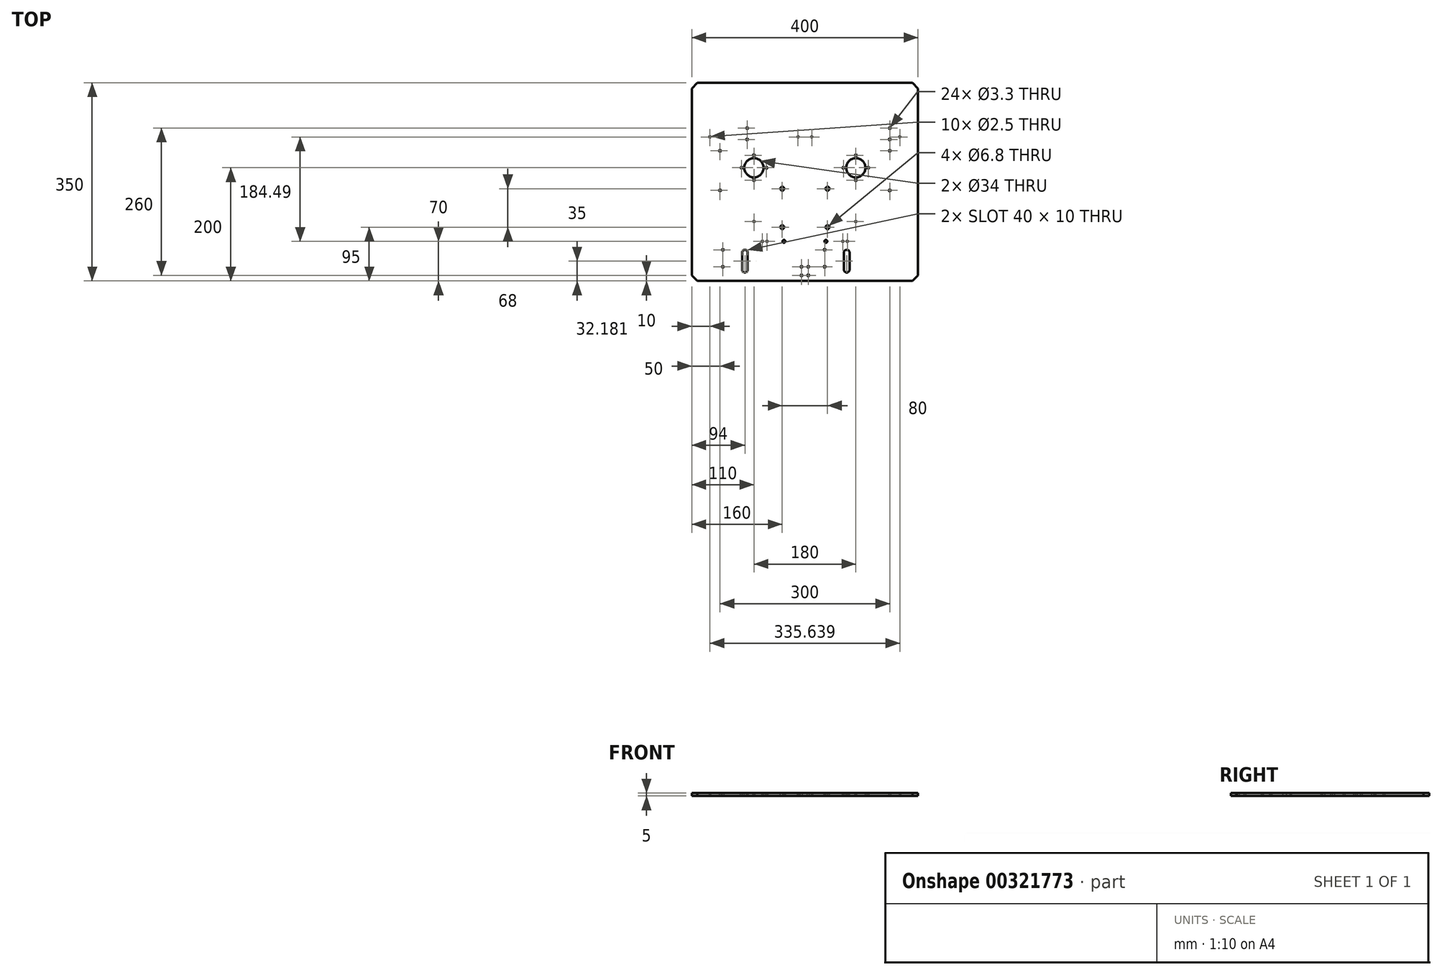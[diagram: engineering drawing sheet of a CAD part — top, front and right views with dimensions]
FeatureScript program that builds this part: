
annotation { "Feature Type Name" : "Feature", "Feature Type Description" : "" }
export const myFeature = defineFeature(function(context is Context, id is Id, definition is map)
    precondition{}
    {
        {
            var Q0;
            Q0=qCreatedBy(makeId("Top.planeOp"),FACE);
            var sketch = newSketch(context, id + "F0", { "sketchPlane" : qUnion([Q0])});
            skLineSegment(sketch, "E0.bottom", {"start": v(-200, 100) * mm, "end": v(200, 100) * mm});
            skLineSegment(sketch, "E0.top", {"start": v(-200, -250) * mm, "end": v(200, -250) * mm});
            skLineSegment(sketch, "E0.left", {"start": v(-200, 100) * mm, "end": v(-200, -250) * mm});
            skLineSegment(sketch, "E0.right", {"start": v(200, 100) * mm, "end": v(200, -250) * mm});
            skSolve(sketch);
        }
        {
            var Q0;
            Q0=qSketchRegion(id+"F0",true);
            extrude(context, id + "F1", {"entities" : qUnion([Q0]), "depth" : 5 * mm});
        }
        {
            var Q0;
            Q0=makeQuery(id+"F1.opExtrude","CAP_FACE",FACE,{"disambiguationData":[OSD([sQuery(id+"F0.wireOp",EDGE,"E0.bottom"),sQuery(id+"F0.wireOp",EDGE,"E0.top"),sQuery(id+"F0.wireOp",EDGE,"E0.left"),sQuery(id+"F0.wireOp",EDGE,"E0.right")])],"isStart":false});
            var sketch = newSketch(context, id + "F2", { "sketchPlane" : qUnion([Q0])});
            skCircle(sketch, "E1", {"center": v(-90, -50) * mm, "radius": 17 * mm});
            skCircle(sketch, "E2", {"center": v(90, -50) * mm, "radius": 17 * mm});
            skSolve(sketch);
        }
        {
            var Q0;
            Q0=qSketchRegion(id+"F2",true);
            extrude(context, id + "F3", {"entities" : qUnion([Q0]), "operationType" : NewBodyOperationType.REMOVE, "oppositeDirection" : true, "depth" : 25 * mm});
        }
        {
            var Q0;
            Q0=makeQuery(id+"F1.opExtrude","CAP_FACE",FACE,{"disambiguationData":[OSD([sQuery(id+"F0.wireOp",EDGE,"E0.bottom"),sQuery(id+"F0.wireOp",EDGE,"E0.top"),sQuery(id+"F0.wireOp",EDGE,"E0.left"),sQuery(id+"F0.wireOp",EDGE,"E0.right")])],"isStart":false});
            var sketch = newSketch(context, id + "F4", { "sketchPlane" : qUnion([Q0])});
            skCircle(sketch, "E3", {"center": v(-90, -50) * mm, "radius": 22 * mm});
            skCircle(sketch, "E4", {"center": v(90, -50) * mm, "radius": 22 * mm});
            skPoint(sketch, "E5", {"position": v(90, -28) * mm});
            skPoint(sketch, "E6", {"position": v(112, -50) * mm});
            skPoint(sketch, "E7", {"position": v(90, -72) * mm});
            skPoint(sketch, "E8", {"position": v(68, -50) * mm});
            skPoint(sketch, "E9", {"position": v(-68, -50) * mm});
            skPoint(sketch, "E10", {"position": v(-90, -28) * mm});
            skPoint(sketch, "E11", {"position": v(-90, -72) * mm});
            skPoint(sketch, "E12", {"position": v(-112, -50) * mm});
            skSolve(sketch);
        }
        {
            var Q0;
            Q0=sQuery(id+"F4.wireOp",VERTEX,"E11");
            var Q1;
            Q1=sQuery(id+"F4.wireOp",VERTEX,"E9");
            var Q2;
            Q2=sQuery(id+"F4.wireOp",VERTEX,"E10");
            var Q3;
            Q3=sQuery(id+"F4.wireOp",VERTEX,"E12");
            var Q4;
            Q4=sQuery(id+"F4.wireOp",VERTEX,"E8");
            var Q5;
            Q5=sQuery(id+"F4.wireOp",VERTEX,"E7");
            var Q6;
            Q6=sQuery(id+"F4.wireOp",VERTEX,"E6");
            var Q7;
            Q7=sQuery(id+"F4.wireOp",VERTEX,"E5");
            var Q8;
            Q8=makeQuery(id+"F1.opExtrude","SWEPT_BODY",BODY,{"disambiguationData":[OSD([sQuery(id+"F0.wireOp",EDGE,"E0.bottom"),sQuery(id+"F0.wireOp",EDGE,"E0.top"),sQuery(id+"F0.wireOp",EDGE,"E0.left"),sQuery(id+"F0.wireOp",EDGE,"E0.right")])]});
            hole(context, id + "F5", {"style" : HoleStyle.SIMPLE, "endStyle" : HoleEndStyle.THROUGH, "standardTappedOrClearance" : lookupTablePath({ "standard" : "ISO", "engagement" : "75%", "pitch" : "0.7 mm", "size" : "M4", "type" : "Tapped" }), "standardBlindInLast" : lookupTablePath({ "standard" : "ISO", "engagement" : "75%", "pitch" : "0.7 mm", "size" : "M4", "type" : "Tapped" }), "holeDiameter" : 3.3 * mm, "locations" : qUnion([Q0, Q1, Q2, Q3, Q4, Q5, Q6, Q7]), "scope" : qUnion([Q8]), "showTappedDepth" : true, "tappedDepth" : 12 * mm, "tapClearance" : 3, "majorDiameter" : 4 * mm});
        }
        {
            var Q0;
            Q0=makeQuery(id+"F1.opExtrude","CAP_FACE",FACE,{"disambiguationData":[OSD([sQuery(id+"F0.wireOp",EDGE,"E0.bottom"),sQuery(id+"F0.wireOp",EDGE,"E0.top"),sQuery(id+"F0.wireOp",EDGE,"E0.left"),sQuery(id+"F0.wireOp",EDGE,"E0.right")])],"isStart":false});
            var sketch = newSketch(context, id + "F6", { "sketchPlane" : qUnion([Q0])});
            skPoint(sketch, "E13", {"position": v(6, -240) * mm});
            skPoint(sketch, "E14", {"position": v(6, -225) * mm});
            skPoint(sketch, "E15", {"position": v(-6, -225) * mm});
            skPoint(sketch, "E16", {"position": v(-6, -240) * mm});
            skSolve(sketch);
        }
        {
            var Q0;
            Q0=sQuery(id+"F6.wireOp",VERTEX,"E15");
            var Q1;
            Q1=sQuery(id+"F6.wireOp",VERTEX,"E14");
            var Q2;
            Q2=sQuery(id+"F6.wireOp",VERTEX,"E13");
            var Q3;
            Q3=sQuery(id+"F6.wireOp",VERTEX,"E16");
            var Q4;
            Q4=makeQuery(id+"F1.opExtrude","SWEPT_BODY",BODY,{"disambiguationData":[OSD([sQuery(id+"F0.wireOp",EDGE,"E0.bottom"),sQuery(id+"F0.wireOp",EDGE,"E0.top"),sQuery(id+"F0.wireOp",EDGE,"E0.left"),sQuery(id+"F0.wireOp",EDGE,"E0.right")])]});
            hole(context, id + "F7", {"style" : HoleStyle.SIMPLE, "endStyle" : HoleEndStyle.THROUGH, "standardTappedOrClearance" : lookupTablePath({ "standard" : "ISO", "engagement" : "75%", "pitch" : "0.7 mm", "size" : "M4", "type" : "Tapped" }), "standardBlindInLast" : lookupTablePath({ "standard" : "ISO", "engagement" : "75%", "pitch" : "0.7 mm", "size" : "M4", "type" : "Tapped" }), "holeDiameter" : 3.3 * mm, "locations" : qUnion([Q0, Q1, Q2, Q3]), "scope" : qUnion([Q4]), "showTappedDepth" : true, "tappedDepth" : 12 * mm, "tapClearance" : 3, "majorDiameter" : 4 * mm});
        }
        {
            var Q0;
            Q0=makeQuery(id+"F1.opExtrude","CAP_FACE",FACE,{"disambiguationData":[OSD([sQuery(id+"F0.wireOp",EDGE,"E0.bottom"),sQuery(id+"F0.wireOp",EDGE,"E0.top"),sQuery(id+"F0.wireOp",EDGE,"E0.left"),sQuery(id+"F0.wireOp",EDGE,"E0.right")])],"isStart":true});
            var sketch = newSketch(context, id + "F8", { "sketchPlane" : qUnion([Q0])});
            skPoint(sketch, "E17", {"position": v(-145, 225) * mm});
            skPoint(sketch, "E18", {"position": v(-145, 195) * mm});
            skPoint(sketch, "E19", {"position": v(35, 225) * mm});
            skPoint(sketch, "E20", {"position": v(35, 195) * mm});
            skSolve(sketch);
        }
        {
            var Q0;
            Q0=sQuery(id+"F8.wireOp",VERTEX,"E17");
            var Q1;
            Q1=sQuery(id+"F8.wireOp",VERTEX,"E18");
            var Q2;
            Q2=sQuery(id+"F8.wireOp",VERTEX,"E20");
            var Q3;
            Q3=sQuery(id+"F8.wireOp",VERTEX,"E19");
            var Q4;
            Q4=makeQuery(id+"F1.opExtrude","SWEPT_BODY",BODY,{"disambiguationData":[OSD([sQuery(id+"F0.wireOp",EDGE,"E0.bottom"),sQuery(id+"F0.wireOp",EDGE,"E0.top"),sQuery(id+"F0.wireOp",EDGE,"E0.left"),sQuery(id+"F0.wireOp",EDGE,"E0.right")])]});
            hole(context, id + "F9", {"style" : HoleStyle.SIMPLE, "endStyle" : HoleEndStyle.THROUGH, "standardTappedOrClearance" : lookupTablePath({ "standard" : "ISO", "engagement" : "75%", "pitch" : "0.7 mm", "size" : "M4", "type" : "Tapped" }), "standardBlindInLast" : lookupTablePath({ "standard" : "ISO", "engagement" : "75%", "pitch" : "0.7 mm", "size" : "M4", "type" : "Tapped" }), "holeDiameter" : 3.3 * mm, "locations" : qUnion([Q0, Q1, Q2, Q3]), "scope" : qUnion([Q4]), "showTappedDepth" : true, "tappedDepth" : 12 * mm, "tapClearance" : 3, "majorDiameter" : 4 * mm});
        }
        {
            var Q0;
            Q0=makeQuery(id+"F1.opExtrude","CAP_FACE",FACE,{"disambiguationData":[OSD([sQuery(id+"F0.wireOp",EDGE,"E0.bottom"),sQuery(id+"F0.wireOp",EDGE,"E0.top"),sQuery(id+"F0.wireOp",EDGE,"E0.left"),sQuery(id+"F0.wireOp",EDGE,"E0.right")])],"isStart":false});
            var sketch = newSketch(context, id + "F10", { "sketchPlane" : qUnion([Q0])});
            skArc(sketch, "E21", {"start": v(-101, -200) * mm, "mid": v(-106, -195) * mm, "end": v(-111, -200) * mm});
            skArc(sketch, "E22", {"start": v(-111, -230) * mm, "mid": v(-106, -235) * mm, "end": v(-101, -230) * mm});
            skArc(sketch, "E23", {"start": v(69, -230) * mm, "mid": v(74, -235) * mm, "end": v(79, -230) * mm});
            skArc(sketch, "E24", {"start": v(79, -200) * mm, "mid": v(74, -195) * mm, "end": v(69, -200) * mm});
            skLineSegment(sketch, "E25", {"start": v(79, -200) * mm, "end": v(79, -230) * mm});
            skLineSegment(sketch, "E26", {"start": v(69, -230) * mm, "end": v(69, -200) * mm});
            skLineSegment(sketch, "E27", {"start": v(-101, -200) * mm, "end": v(-101, -230) * mm});
            skLineSegment(sketch, "E28", {"start": v(-111, -230) * mm, "end": v(-111, -200) * mm});
            skSolve(sketch);
        }
        {
            var Q0;
            Q0=qSketchRegion(id+"F10",true);
            extrude(context, id + "F11", {"entities" : qUnion([Q0]), "operationType" : NewBodyOperationType.REMOVE, "oppositeDirection" : true, "depth" : 25 * mm});
        }
        {
            var Q0;
            Q0=makeQuery(id+"F1.opExtrude","CAP_FACE",FACE,{"disambiguationData":[OSD([sQuery(id+"F0.wireOp",EDGE,"E0.bottom"),sQuery(id+"F0.wireOp",EDGE,"E0.top"),sQuery(id+"F0.wireOp",EDGE,"E0.left"),sQuery(id+"F0.wireOp",EDGE,"E0.right")])],"isStart":true});
            var sketch = newSketch(context, id + "F12", { "sketchPlane" : qUnion([Q0])});
            skPoint(sketch, "E29", {"position": v(-102, 0) * mm});
            skPoint(sketch, "E30", {"position": v(-102, -20) * mm});
            skPoint(sketch, "E31", {"position": v(150, 0) * mm});
            skPoint(sketch, "E32", {"position": v(150, -20) * mm});
            skSolve(sketch);
        }
        {
            var Q0;
            Q0=sQuery(id+"F12.wireOp",VERTEX,"E30");
            var Q1;
            Q1=sQuery(id+"F12.wireOp",VERTEX,"E29");
            var Q2;
            Q2=sQuery(id+"F12.wireOp",VERTEX,"E31");
            var Q3;
            Q3=sQuery(id+"F12.wireOp",VERTEX,"E32");
            var Q4;
            Q4=makeQuery(id+"F1.opExtrude","SWEPT_BODY",BODY,{"disambiguationData":[OSD([sQuery(id+"F0.wireOp",EDGE,"E0.bottom"),sQuery(id+"F0.wireOp",EDGE,"E0.top"),sQuery(id+"F0.wireOp",EDGE,"E0.left"),sQuery(id+"F0.wireOp",EDGE,"E0.right")])]});
            hole(context, id + "F13", {"style" : HoleStyle.SIMPLE, "endStyle" : HoleEndStyle.THROUGH, "standardTappedOrClearance" : lookupTablePath({ "standard" : "ISO", "engagement" : "75%", "pitch" : "0.7 mm", "size" : "M4", "type" : "Tapped" }), "standardBlindInLast" : lookupTablePath({ "standard" : "ISO", "engagement" : "75%", "pitch" : "0.7 mm", "size" : "M4", "type" : "Tapped" }), "holeDiameter" : 3.3 * mm, "locations" : qUnion([Q0, Q1, Q2, Q3]), "scope" : qUnion([Q4]), "showTappedDepth" : true, "tappedDepth" : 12 * mm, "tapClearance" : 3, "majorDiameter" : 4 * mm});
        }
        {
            var Q0;
            Q0=makeQuery(id+"F1.opExtrude","CAP_FACE",FACE,{"disambiguationData":[OSD([sQuery(id+"F0.wireOp",EDGE,"E0.bottom"),sQuery(id+"F0.wireOp",EDGE,"E0.top"),sQuery(id+"F0.wireOp",EDGE,"E0.left"),sQuery(id+"F0.wireOp",EDGE,"E0.right")])],"isStart":true});
            var sketch = newSketch(context, id + "F14", { "sketchPlane" : qUnion([Q0])});
            skPoint(sketch, "E33", {"position": v(-150, 20) * mm});
            skPoint(sketch, "E34", {"position": v(-150, 90) * mm});
            skPoint(sketch, "E35", {"position": v(150, 90) * mm});
            skPoint(sketch, "E36", {"position": v(150, 20) * mm});
            skSolve(sketch);
        }
        {
            var Q0;
            Q0=sQuery(id+"F14.wireOp",VERTEX,"E33");
            var Q1;
            Q1=sQuery(id+"F14.wireOp",VERTEX,"E34");
            var Q2;
            Q2=sQuery(id+"F14.wireOp",VERTEX,"E35");
            var Q3;
            Q3=sQuery(id+"F14.wireOp",VERTEX,"E36");
            var Q4;
            Q4=makeQuery(id+"F1.opExtrude","SWEPT_BODY",BODY,{"disambiguationData":[OSD([sQuery(id+"F0.wireOp",EDGE,"E0.bottom"),sQuery(id+"F0.wireOp",EDGE,"E0.top"),sQuery(id+"F0.wireOp",EDGE,"E0.left"),sQuery(id+"F0.wireOp",EDGE,"E0.right")])]});
            hole(context, id + "F15", {"style" : HoleStyle.SIMPLE, "endStyle" : HoleEndStyle.THROUGH, "standardTappedOrClearance" : lookupTablePath({ "standard" : "ISO", "engagement" : "75%", "pitch" : "0.7 mm", "size" : "M4", "type" : "Tapped" }), "standardBlindInLast" : lookupTablePath({ "standard" : "ISO", "engagement" : "75%", "pitch" : "0.7 mm", "size" : "M4", "type" : "Tapped" }), "holeDiameter" : 3.3 * mm, "locations" : qUnion([Q0, Q1, Q2, Q3]), "scope" : qUnion([Q4]), "showTappedDepth" : true, "tappedDepth" : 12 * mm, "tapClearance" : 3, "majorDiameter" : 4 * mm});
        }
        {
            var Q0;
            Q0=makeQuery(id+"F1.opExtrude","CAP_FACE",FACE,{"disambiguationData":[OSD([sQuery(id+"F0.wireOp",EDGE,"E0.bottom"),sQuery(id+"F0.wireOp",EDGE,"E0.top"),sQuery(id+"F0.wireOp",EDGE,"E0.left"),sQuery(id+"F0.wireOp",EDGE,"E0.right")])],"isStart":true});
            var sketch = newSketch(context, id + "F16", { "sketchPlane" : qUnion([Q0])});
            skPoint(sketch, "E37", {"position": v(-75, 180) * mm});
            skPoint(sketch, "E38", {"position": v(75, 180) * mm});
            skPoint(sketch, "E39", {"position": v(67, 180) * mm});
            skPoint(sketch, "E40", {"position": v(-67, 180) * mm});
            skPoint(sketch, "E41", {"position": v(-37, 180) * mm});
            skPoint(sketch, "E42", {"position": v(37, 180) * mm});
            skSolve(sketch);
        }
        {
            var Q0;
            Q0=sQuery(id+"F16.wireOp",VERTEX,"E37");
            var Q1;
            Q1=sQuery(id+"F16.wireOp",VERTEX,"E40");
            var Q2;
            Q2=sQuery(id+"F16.wireOp",VERTEX,"E39");
            var Q3;
            Q3=sQuery(id+"F16.wireOp",VERTEX,"E38");
            var Q4;
            Q4=makeQuery(id+"F1.opExtrude","SWEPT_BODY",BODY,{"disambiguationData":[OSD([sQuery(id+"F0.wireOp",EDGE,"E0.bottom"),sQuery(id+"F0.wireOp",EDGE,"E0.top"),sQuery(id+"F0.wireOp",EDGE,"E0.left"),sQuery(id+"F0.wireOp",EDGE,"E0.right")])]});
            hole(context, id + "F17", {"style" : HoleStyle.SIMPLE, "endStyle" : HoleEndStyle.THROUGH, "standardTappedOrClearance" : lookupTablePath({ "standard" : "ISO", "engagement" : "75%", "pitch" : "0.5 mm", "size" : "M3", "type" : "Tapped" }), "standardBlindInLast" : lookupTablePath({ "standard" : "ISO", "engagement" : "75%", "pitch" : "0.5 mm", "size" : "M3", "type" : "Tapped" }), "holeDiameter" : 2.5 * mm, "locations" : qUnion([Q0, Q1, Q2, Q3]), "scope" : qUnion([Q4]), "showTappedDepth" : true, "tappedDepth" : 12 * mm, "tapClearance" : 3, "majorDiameter" : 3 * mm});
        }
        {
            var Q0;
            Q0=sQuery(id+"F16.wireOp",VERTEX,"E41");
            var Q1;
            Q1=sQuery(id+"F16.wireOp",VERTEX,"E42");
            var Q2;
            Q2=makeQuery(id+"F1.opExtrude","SWEPT_BODY",BODY,{"disambiguationData":[OSD([sQuery(id+"F0.wireOp",EDGE,"E0.bottom"),sQuery(id+"F0.wireOp",EDGE,"E0.top"),sQuery(id+"F0.wireOp",EDGE,"E0.left"),sQuery(id+"F0.wireOp",EDGE,"E0.right")])]});
            hole(context, id + "F18", {"style" : HoleStyle.SIMPLE, "endStyle" : HoleEndStyle.THROUGH, "holeDiameter" : 5 * mm, "locations" : qUnion([Q0, Q1]), "scope" : qUnion([Q2]), "tappedDepth" : 12 * mm, "tapClearance" : 3});
        }
        {
            var Q0;
            Q0=makeQuery(id+"F1.opExtrude","CAP_FACE",FACE,{"disambiguationData":[OSD([sQuery(id+"F0.wireOp",EDGE,"E0.bottom"),sQuery(id+"F0.wireOp",EDGE,"E0.top"),sQuery(id+"F0.wireOp",EDGE,"E0.left"),sQuery(id+"F0.wireOp",EDGE,"E0.right")])],"isStart":true});
            var sketch = newSketch(context, id + "F19", { "sketchPlane" : qUnion([Q0])});
            skCircle(sketch, "E43", {"center": v(-90, 50) * mm, "radius": 95 * mm});
            skPoint(sketch, "E44", {"position": v(-90, 145) * mm});
            skLineSegment(sketch, "E45", {"start": v(-90, 50) * mm, "end": v(-175.07, -9.56) * mm});
            skLineSegment(sketch, "E46", {"start": v(-90, 50) * mm, "end": v(6.25, -17.4) * mm});
            skPoint(sketch, "E47", {"position": v(-167.82, -4.49) * mm});
            skPoint(sketch, "E48", {"position": v(-12.18, -4.49) * mm});
            skCircle(sketch, "E49", {"center": v(90, 50) * mm, "radius": 95 * mm});
            skLineSegment(sketch, "E50", {"start": v(90, 50) * mm, "end": v(186.69, -17.7) * mm});
            skLineSegment(sketch, "E51", {"start": v(90, 50) * mm, "end": v(-14.47, -23.15) * mm});
            skPoint(sketch, "E52", {"position": v(12.18, -4.49) * mm});
            skPoint(sketch, "E53", {"position": v(167.82, -4.49) * mm});
            skLineSegment(sketch, "E54", {"start": v(-90, 28) * mm, "end": v(-90, 72) * mm});
            skLineSegment(sketch, "E55", {"start": v(90, 28) * mm, "end": v(90, 72) * mm});
            skPoint(sketch, "E56", {"position": v(90, 145) * mm});
            skSolve(sketch);
        }
        {
            var Q0;
            Q0=sQuery(id+"F19.wireOp",VERTEX,"E47");
            var Q1;
            Q1=sQuery(id+"F19.wireOp",VERTEX,"E48");
            var Q2;
            Q2=sQuery(id+"F19.wireOp",VERTEX,"E44");
            var Q3;
            Q3=sQuery(id+"F19.wireOp",VERTEX,"E52");
            var Q4;
            Q4=sQuery(id+"F19.wireOp",VERTEX,"E53");
            var Q5;
            Q5=sQuery(id+"F19.wireOp",VERTEX,"E56");
            var Q6;
            Q6=makeQuery(id+"F1.opExtrude","SWEPT_BODY",BODY,{"disambiguationData":[OSD([sQuery(id+"F0.wireOp",EDGE,"E0.bottom"),sQuery(id+"F0.wireOp",EDGE,"E0.top"),sQuery(id+"F0.wireOp",EDGE,"E0.left"),sQuery(id+"F0.wireOp",EDGE,"E0.right")])]});
            hole(context, id + "F20", {"style" : HoleStyle.SIMPLE, "endStyle" : HoleEndStyle.THROUGH, "standardTappedOrClearance" : lookupTablePath({ "standard" : "ISO", "engagement" : "75%", "pitch" : "0.5 mm", "size" : "M3", "type" : "Tapped" }), "standardBlindInLast" : lookupTablePath({ "standard" : "ISO", "engagement" : "75%", "pitch" : "0.5 mm", "size" : "M3", "type" : "Tapped" }), "holeDiameter" : 2.5 * mm, "locations" : qUnion([Q0, Q1, Q2, Q3, Q4, Q5]), "scope" : qUnion([Q6]), "showTappedDepth" : true, "tappedDepth" : 12 * mm, "tapClearance" : 3, "majorDiameter" : 3 * mm});
        }
        {
            var Q0;
            Q0=makeQuery(id+"F1.opExtrude","CAP_FACE",FACE,{"disambiguationData":[OSD([sQuery(id+"F0.wireOp",EDGE,"E0.bottom"),sQuery(id+"F0.wireOp",EDGE,"E0.top"),sQuery(id+"F0.wireOp",EDGE,"E0.left"),sQuery(id+"F0.wireOp",EDGE,"E0.right")])],"isStart":false});
            var sketch = newSketch(context, id + "F21", { "sketchPlane" : qUnion([Q0])});
            skPoint(sketch, "E57", {"position": v(-40, -155) * mm});
            skPoint(sketch, "E58", {"position": v(40, -155) * mm});
            skPoint(sketch, "E59", {"position": v(40, -87) * mm});
            skPoint(sketch, "E60", {"position": v(-40, -87) * mm});
            skSolve(sketch);
        }
        {
            var Q0;
            Q0=sQuery(id+"F21.wireOp",VERTEX,"E60");
            var Q1;
            Q1=sQuery(id+"F21.wireOp",VERTEX,"E57");
            var Q2;
            Q2=sQuery(id+"F21.wireOp",VERTEX,"E58");
            var Q3;
            Q3=sQuery(id+"F21.wireOp",VERTEX,"E59");
            var Q4;
            Q4=makeQuery(id+"F1.opExtrude","SWEPT_BODY",BODY,{"disambiguationData":[OSD([sQuery(id+"F0.wireOp",EDGE,"E0.bottom"),sQuery(id+"F0.wireOp",EDGE,"E0.top"),sQuery(id+"F0.wireOp",EDGE,"E0.left"),sQuery(id+"F0.wireOp",EDGE,"E0.right")])]});
            hole(context, id + "F22", {"style" : HoleStyle.SIMPLE, "endStyle" : HoleEndStyle.THROUGH, "standardTappedOrClearance" : lookupTablePath({ "standard" : "ISO", "engagement" : "75%", "pitch" : "1.25 mm", "size" : "M8", "type" : "Tapped" }), "standardBlindInLast" : lookupTablePath({ "standard" : "ISO", "engagement" : "75%", "pitch" : "1.25 mm", "size" : "M8", "type" : "Tapped" }), "holeDiameter" : 6.8 * mm, "locations" : qUnion([Q0, Q1, Q2, Q3]), "scope" : qUnion([Q4]), "showTappedDepth" : true, "tappedDepth" : 12 * mm, "tapClearance" : 3, "majorDiameter" : 8 * mm});
        }
        {
            var Q0;
            Q0=makeQuery(id+"F1.opExtrude","SWEPT_EDGE",EDGE,{"disambiguationData":[OSD([sQuery(id+"F0.wireOp",EDGE,"E0.top"),sQuery(id+"F0.wireOp",EDGE,"E0.left")])]});
            var Q1;
            Q1=makeQuery(id+"F1.opExtrude","SWEPT_EDGE",EDGE,{"disambiguationData":[OSD([sQuery(id+"F0.wireOp",EDGE,"E0.top"),sQuery(id+"F0.wireOp",EDGE,"E0.right")])]});
            var Q2;
            Q2=makeQuery(id+"F1.opExtrude","SWEPT_EDGE",EDGE,{"disambiguationData":[OSD([sQuery(id+"F0.wireOp",EDGE,"E0.bottom"),sQuery(id+"F0.wireOp",EDGE,"E0.right")])]});
            var Q3;
            Q3=makeQuery(id+"F1.opExtrude","SWEPT_EDGE",EDGE,{"disambiguationData":[OSD([sQuery(id+"F0.wireOp",EDGE,"E0.bottom"),sQuery(id+"F0.wireOp",EDGE,"E0.left")])]});
            chamfer(context, id + "F23", {"entities" : qUnion([Q0, Q1, Q2, Q3]), "width" : 10 * mm, "tangentPropagation" : true});
        }
    });
